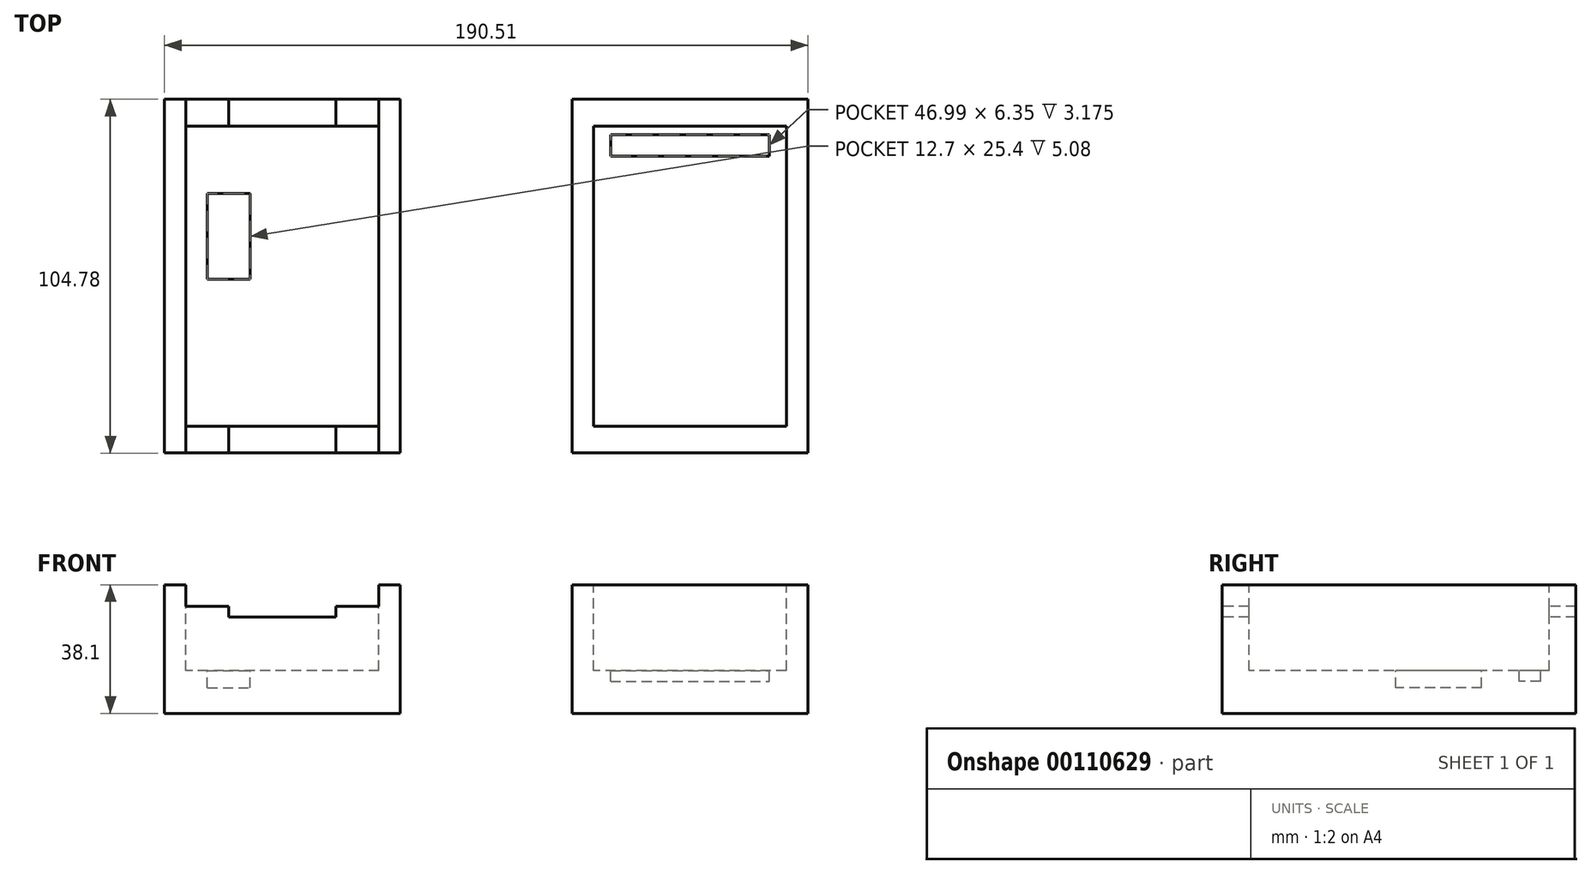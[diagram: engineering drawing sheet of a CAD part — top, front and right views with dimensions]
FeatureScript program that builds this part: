
annotation { "Feature Type Name" : "Feature", "Feature Type Description" : "" }
export const myFeature = defineFeature(function(context is Context, id is Id, definition is map)
    precondition{}
    {
        {
            var Q0;
            Q0=qCreatedBy(makeId("Top.planeOp"),FACE);
            var sketch = newSketch(context, id + "F0", { "sketchPlane" : qUnion([Q0])});
            skLineSegment(sketch, "E0.bottom", {"start": v(34.93, 52.39) * mm, "end": v(-34.92, 52.39) * mm});
            skLineSegment(sketch, "E0.top", {"start": v(34.93, -52.39) * mm, "end": v(-34.93, -52.39) * mm});
            skLineSegment(sketch, "E0.left", {"start": v(34.93, 52.39) * mm, "end": v(34.92, -52.39) * mm});
            skLineSegment(sketch, "E0.right", {"start": v(-34.92, 52.39) * mm, "end": v(-34.93, -52.39) * mm});
            skPoint(sketch, "E0.middle", {"position": v(0, 0) * mm});
            skLineSegment(sketch, "E1.bottom", {"start": v(-85.74, 52.39) * mm, "end": v(-155.6, 52.39) * mm});
            skLineSegment(sketch, "E1.top", {"start": v(-85.74, -52.39) * mm, "end": v(-155.6, -52.39) * mm});
            skLineSegment(sketch, "E1.left", {"start": v(-85.74, 52.39) * mm, "end": v(-85.74, -52.39) * mm});
            skLineSegment(sketch, "E1.right", {"start": v(-155.6, 52.39) * mm, "end": v(-155.6, -52.39) * mm});
            skPoint(sketch, "E1.middle", {"position": v(-120.67, 0) * mm});
            skSolve(sketch);
        }
        {
            var Q0;
            Q0=qSketchRegion(id+"F0",true);
            extrude(context, id + "F1", {"entities" : qUnion([Q0]), "oppositeDirection" : true, "depth" : 38.1 * mm});
        }
        {
            var Q0;
            Q0=qCreatedBy(makeId("Top.planeOp"),FACE);
            var sketch = newSketch(context, id + "F2", { "sketchPlane" : qUnion([Q0])});
            skLineSegment(sketch, "E2.bottom", {"start": v(28.58, 44.45) * mm, "end": v(-28.58, 44.45) * mm});
            skLineSegment(sketch, "E2.top", {"start": v(28.58, -44.45) * mm, "end": v(-28.58, -44.45) * mm});
            skLineSegment(sketch, "E2.left", {"start": v(28.58, 44.45) * mm, "end": v(28.58, -44.45) * mm});
            skLineSegment(sketch, "E2.right", {"start": v(-28.58, 44.45) * mm, "end": v(-28.58, -44.45) * mm});
            skPoint(sketch, "E2.middle", {"position": v(0, 0) * mm});
            skLineSegment(sketch, "E3.bottom", {"start": v(-92.1, 44.45) * mm, "end": v(-149.24, 44.45) * mm});
            skLineSegment(sketch, "E3.top", {"start": v(-92.1, -44.45) * mm, "end": v(-149.24, -44.45) * mm});
            skLineSegment(sketch, "E3.left", {"start": v(-92.1, 44.45) * mm, "end": v(-92.1, -44.45) * mm});
            skLineSegment(sketch, "E3.right", {"start": v(-149.24, 44.45) * mm, "end": v(-149.24, -44.45) * mm});
            skPoint(sketch, "E3.middle", {"position": v(-120.67, 0) * mm});
            skPoint(sketch, "E3.middle.positionSnap0", {"position": v(-28.58, 0) * mm});
            skPoint(sketch, "E3.centerSnap0", {"position": v(-28.58, 0) * mm});
            skLineSegment(sketch, "E4", {"start": v(-92.1, 44.45) * mm, "end": v(-85.74, 44.45) * mm, "construction": true});
            skLineSegment(sketch, "E5", {"start": v(-149.24, 44.45) * mm, "end": v(-155.6, 44.45) * mm, "construction": true});
            skSolve(sketch);
        }
        {
            var Q0;
            Q0=makeQuery(id+"F2.imprint","IMPRINT",FACE,{"disambiguationData":[TD([[makeQuery(id+"F2.imprint","IMPRINT",EDGE,{"derivedFrom":sQuery(id+"F2.wireOp",EDGE,"E2.bottom")}),1.0]])]});
            var Q1;
            Q1=sQuery(id+"F2.wireOp",EDGE,"E3.right");
            var Q2;
            Q2=sQuery(id+"F2.wireOp",EDGE,"E3.bottom");
            var Q3;
            Q3=sQuery(id+"F2.wireOp",EDGE,"E3.left");
            var Q4;
            Q4=sQuery(id+"F2.wireOp",EDGE,"E3.top");
            var Q5;
            Q5=sQuery(id+"F2.wireOp",EDGE,"E2.bottom");
            var Q6;
            Q6=sQuery(id+"F2.wireOp",EDGE,"E2.right");
            var Q7;
            Q7=sQuery(id+"F2.wireOp",EDGE,"E2.left");
            var Q8;
            Q8=sQuery(id+"F2.wireOp",EDGE,"E2.top");
            extrude(context, id + "F3", {"entities" : qUnion([Q0]), "operationType" : NewBodyOperationType.REMOVE, "surfaceEntities" : qUnion([Q1, Q2, Q3, Q4, Q5, Q6, Q7, Q8]), "oppositeDirection" : true, "depth" : 25.4 * mm});
        }
        {
            var Q0;
            Q0=makeQuery(id+"F3.boolean.opBoolean","COPY",FACE,{"derivedFrom":makeQuery(id+"F3.opExtrude","CAP_FACE",FACE,{"disambiguationData":[OSD([sQuery(id+"F2.wireOp",EDGE,"E2.bottom"),sQuery(id+"F2.wireOp",EDGE,"E2.top"),sQuery(id+"F2.wireOp",EDGE,"E2.left"),sQuery(id+"F2.wireOp",EDGE,"E2.right")])],"isStart":false})});
            var sketch = newSketch(context, id + "F4", { "sketchPlane" : qUnion([Q0])});
            skLineSegment(sketch, "E6.bottom", {"start": v(-28.58, -44.45) * mm, "end": v(28.58, -44.45) * mm});
            skLineSegment(sketch, "E6.top", {"start": v(-28.58, -19.05) * mm, "end": v(28.58, -19.05) * mm});
            skLineSegment(sketch, "E6.left", {"start": v(-28.58, -44.45) * mm, "end": v(-28.58, -19.05) * mm});
            skLineSegment(sketch, "E6.right", {"start": v(28.58, -44.45) * mm, "end": v(28.58, -19.05) * mm});
            skSolve(sketch);
        }
        {
            var Q0;
            Q0=qSketchRegion(id+"F4",true);
            extrude(context, id + "F5", {"entities" : qUnion([Q0]), "operationType" : NewBodyOperationType.ADD, "depth" : 12.7 * mm});
        }
        {
            var Q0;
            Q0=qSketchRegion(id+"F2",true);
            extrude(context, id + "F6", {"entities" : qUnion([Q0]), "operationType" : NewBodyOperationType.REMOVE, "oppositeDirection" : true, "depth" : 25.4 * mm});
        }
        {
            var Q0;
            Q0=makeQuery(id+"F1.opExtrude","SWEPT_FACE",FACE,{"disambiguationData":[OSD([sQuery(id+"F0.wireOp",EDGE,"E1.top")])]});
            var sketch = newSketch(context, id + "F7", { "sketchPlane" : qUnion([Q0])});
            skLineSegment(sketch, "E7", {"start": v(-149.24, 0) * mm, "end": v(-149.24, -6.35) * mm});
            skLineSegment(sketch, "E8", {"start": v(-149.24, -6.35) * mm, "end": v(-136.54, -6.35) * mm});
            skLineSegment(sketch, "E9", {"start": v(-136.54, -6.35) * mm, "end": v(-136.54, -9.53) * mm});
            skLineSegment(sketch, "E10", {"start": v(-136.54, -9.53) * mm, "end": v(-104.8, -9.53) * mm});
            skLineSegment(sketch, "E11", {"start": v(-104.8, -9.53) * mm, "end": v(-104.8, -6.35) * mm});
            skLineSegment(sketch, "E12", {"start": v(-104.8, -6.35) * mm, "end": v(-92.1, -6.35) * mm});
            skLineSegment(sketch, "E13", {"start": v(-92.1, -6.35) * mm, "end": v(-92.1, 0) * mm});
            skLineSegment(sketch, "E14", {"start": v(-92.1, 0) * mm, "end": v(-149.24, 0) * mm});
            skSolve(sketch);
        }
        {
            var Q0;
            Q0=qSketchRegion(id+"F7",true);
            extrude(context, id + "F8", {"entities" : qUnion([Q0]), "operationType" : NewBodyOperationType.REMOVE, "endBound" : BoundingType.THROUGH_ALL, "oppositeDirection" : true, "depth" : 25.4 * mm});
        }
        {
            var Q0;
            Q0=makeQuery(id+"F6.boolean.opBoolean","COPY",FACE,{"derivedFrom":makeQuery(id+"F6.opExtrude","CAP_FACE",FACE,{"disambiguationData":[OSD([sQuery(id+"F2.wireOp",EDGE,"E3.bottom"),sQuery(id+"F2.wireOp",EDGE,"E3.top"),sQuery(id+"F2.wireOp",EDGE,"E3.left"),sQuery(id+"F2.wireOp",EDGE,"E3.right")])],"isStart":false})});
            var sketch = newSketch(context, id + "F9", { "sketchPlane" : qUnion([Q0])});
            skLineSegment(sketch, "E15.bottom", {"start": v(-142.9, 24.45) * mm, "end": v(-130.2, 24.45) * mm});
            skLineSegment(sketch, "E15.top", {"start": v(-142.9, -0.95) * mm, "end": v(-130.2, -0.95) * mm});
            skLineSegment(sketch, "E15.left", {"start": v(-142.9, 24.45) * mm, "end": v(-142.9, -0.95) * mm});
            skLineSegment(sketch, "E15.right", {"start": v(-130.2, 24.45) * mm, "end": v(-130.2, -0.95) * mm});
            skSolve(sketch);
        }
        {
            var Q0;
            Q0=qSketchRegion(id+"F9",true);
            extrude(context, id + "F10", {"entities" : qUnion([Q0]), "operationType" : NewBodyOperationType.REMOVE, "oppositeDirection" : true, "depth" : 5.08 * mm});
        }
        {
            var Q0;
            Q0=makeQuery(id+"F3.boolean.opBoolean","COPY",FACE,{"derivedFrom":makeQuery(id+"F3.opExtrude","CAP_FACE",FACE,{"disambiguationData":[OSD([sQuery(id+"F2.wireOp",EDGE,"E2.bottom"),sQuery(id+"F2.wireOp",EDGE,"E2.top"),sQuery(id+"F2.wireOp",EDGE,"E2.left"),sQuery(id+"F2.wireOp",EDGE,"E2.right")])],"isStart":false})});
            var sketch = newSketch(context, id + "F11", { "sketchPlane" : qUnion([Q0])});
            skLineSegment(sketch, "E16.bottom", {"start": v(-23.5, 41.91) * mm, "end": v(23.5, 41.91) * mm});
            skLineSegment(sketch, "E16.top", {"start": v(-23.5, 35.56) * mm, "end": v(23.5, 35.56) * mm});
            skLineSegment(sketch, "E16.left", {"start": v(-23.5, 41.91) * mm, "end": v(-23.5, 35.56) * mm});
            skLineSegment(sketch, "E16.right", {"start": v(23.5, 41.91) * mm, "end": v(23.5, 35.56) * mm});
            skPoint(sketch, "E17", {"position": v(0, 35.56) * mm});
            skSolve(sketch);
        }
        {
            var Q0;
            Q0=qSketchRegion(id+"F11",true);
            extrude(context, id + "F12", {"entities" : qUnion([Q0]), "operationType" : NewBodyOperationType.REMOVE, "oppositeDirection" : true, "depth" : 3.17 * mm});
        }
    });
